# Revit family: 206_Finnera Plus-lapivienti
name_source: partatom
category: Duct Accessories
units: mm (PartAtom-declared; Revit-internal decimal feet)

## family parameters
Always vertical = Yes
Cut with Voids When Loaded = No
Part Type = Breaks Into
Round Connector Dimension = Use Diameter
Shared = No
Work Plane-Based = No

## types (1)
- VILPE FINNERA PASS-THROUGH
    CAT0 = Yes
    D = 110 mm
    H2 = 179 mm  [stored 0.58727 ft]
    H2D = 358 mm
    H3 = 20 mm  [stored 0.0656168 ft]
    H4 = 250 mm  [stored 0.82021 ft]
    H41 = 115 mm  [stored 0.377297 ft]
    H5 = 19 mm  [stored 0.062336 ft]
    L = 10 mm  [stored 0.0328084 ft]
    L2 = 5 mm  [stored 0.0164042 ft]
    L2D = 10 mm  [stored 0.0328084 ft]
    MC Product Code = VILPE FINNERA PASS-THROUGH
    Manufacturer = Vilpe
    QmdConnectorList = 201;D;202;D
    S = 20 mm  [stored 0.0656168 ft]
    URL = http://www.vilpe.com
    W2 = 125 mm  [stored 0.410105 ft]
    W22 = 124 mm
    W2D = 249 mm
    W3 = 87 mm  [stored 0.285433 ft]
    W32 = 86 mm  [stored 0.282152 ft]
    magiPartTypeId = 206
    magiProductFamilyId = Finnera Plus-lapivienti
    magiProductId = Finnera Plus-lapivienti

note: [stored X ft] marks values corroborated as IEEE doubles in the binary element streams (Revit-internal decimal feet)

## geometry (parser evidence)
native form markers: Sweep x2
no freeform markers — native parametric forms only
